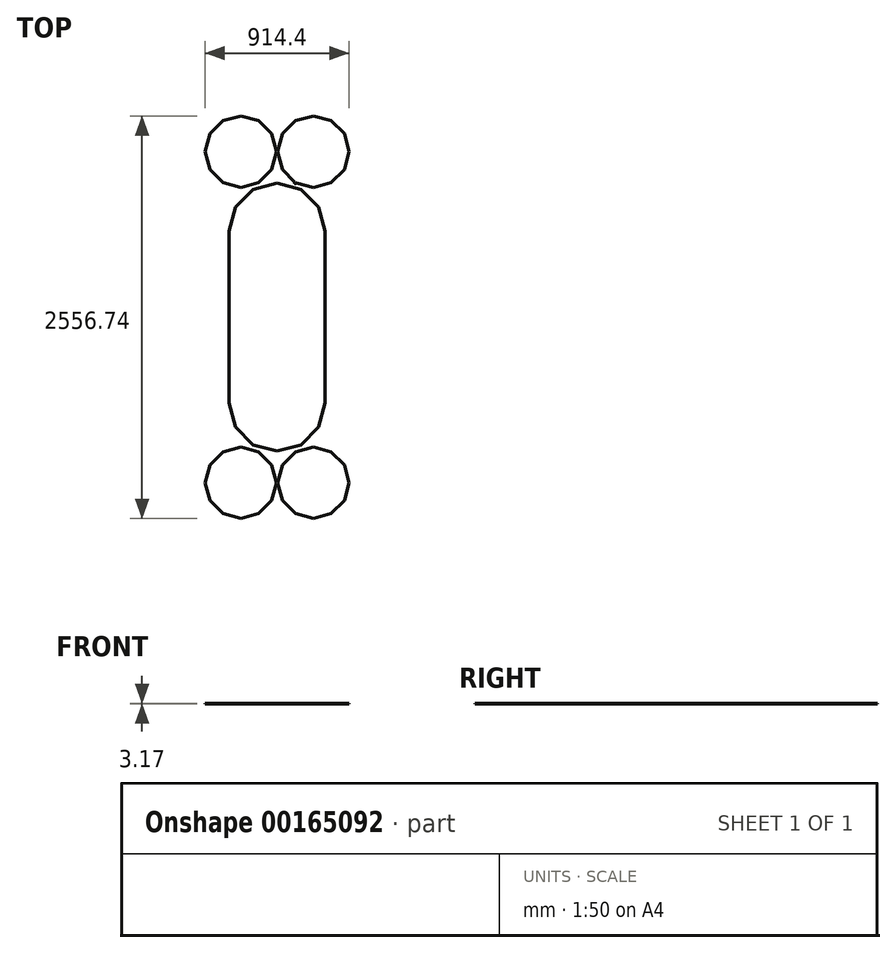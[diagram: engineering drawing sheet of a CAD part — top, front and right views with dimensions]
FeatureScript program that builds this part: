
annotation { "Feature Type Name" : "Feature", "Feature Type Description" : "" }
export const myFeature = defineFeature(function(context is Context, id is Id, definition is map)
    precondition{}
    {
        {
            var Q0;
            Q0=qCreatedBy(makeId("Top.planeOp"),FACE);
            var sketch = newSketch(context, id + "F0", { "sketchPlane" : qUnion([Q0])});
            skLineSegment(sketch, "E0", {"start": v(304.8, 0) * mm, "end": v(609.6, 0) * mm, "construction": true});
            skLineSegment(sketch, "E1", {"start": v(304.8, 0) * mm, "end": v(568.76, 152.4) * mm, "construction": true});
            skLineSegment(sketch, "E2", {"start": v(304.8, 0) * mm, "end": v(457.2, 263.96) * mm, "construction": true});
            skLineSegment(sketch, "E3", {"start": v(304.8, 0) * mm, "end": v(304.8, 304.8) * mm, "construction": true});
            skLineSegment(sketch, "E4", {"start": v(609.6, 0) * mm, "end": v(568.76, 152.4) * mm});
            skLineSegment(sketch, "E5", {"start": v(568.76, 152.4) * mm, "end": v(457.2, 263.96) * mm});
            skLineSegment(sketch, "E6", {"start": v(457.2, 263.96) * mm, "end": v(304.8, 304.8) * mm});
            skLineSegment(sketch, "E7", {"start": v(609.6, 0) * mm, "end": v(609.6, -1092.2) * mm});
            skLineSegment(sketch, "E8", {"start": v(609.6, -1092.2) * mm, "end": v(304.8, -1092.2) * mm, "construction": true});
            skLineSegment(sketch, "E9", {"start": v(304.8, -1092.2) * mm, "end": v(568.76, -1244.6) * mm, "construction": true});
            skLineSegment(sketch, "E10", {"start": v(304.8, 0) * mm, "end": v(152.4, 263.96) * mm, "construction": true});
            skLineSegment(sketch, "E11", {"start": v(304.8, 0) * mm, "end": v(40.84, 152.4) * mm, "construction": true});
            skLineSegment(sketch, "E12", {"start": v(304.8, 0) * mm, "end": v(0, 0) * mm, "construction": true});
            skLineSegment(sketch, "E13", {"start": v(304.8, -1092.2) * mm, "end": v(0, -1092.2) * mm, "construction": true});
            skLineSegment(sketch, "E14", {"start": v(304.8, 304.8) * mm, "end": v(152.4, 263.96) * mm});
            skLineSegment(sketch, "E15", {"start": v(152.4, 263.96) * mm, "end": v(40.84, 152.4) * mm});
            skLineSegment(sketch, "E16", {"start": v(40.84, 152.4) * mm, "end": v(0, 0) * mm});
            skLineSegment(sketch, "E17", {"start": v(0, 0) * mm, "end": v(0, -1092.2) * mm});
            skLineSegment(sketch, "E18", {"start": v(304.8, -1092.2) * mm, "end": v(457.2, -1356.16) * mm, "construction": true});
            skLineSegment(sketch, "E19", {"start": v(304.8, -1092.2) * mm, "end": v(304.8, -1397) * mm, "construction": true});
            skLineSegment(sketch, "E20", {"start": v(304.8, -1092.2) * mm, "end": v(152.4, -1356.16) * mm, "construction": true});
            skLineSegment(sketch, "E21", {"start": v(304.8, -1092.2) * mm, "end": v(40.84, -1244.6) * mm, "construction": true});
            skLineSegment(sketch, "E22", {"start": v(0, -1092.2) * mm, "end": v(40.84, -1244.6) * mm});
            skLineSegment(sketch, "E23", {"start": v(40.84, -1244.6) * mm, "end": v(152.4, -1356.16) * mm});
            skLineSegment(sketch, "E24", {"start": v(152.4, -1356.16) * mm, "end": v(304.8, -1397) * mm});
            skLineSegment(sketch, "E25", {"start": v(304.8, -1397) * mm, "end": v(457.2, -1356.16) * mm});
            skLineSegment(sketch, "E26", {"start": v(457.2, -1356.16) * mm, "end": v(568.76, -1244.6) * mm});
            skLineSegment(sketch, "E27", {"start": v(568.76, -1244.6) * mm, "end": v(609.6, -1092.2) * mm});
            skLineSegment(sketch, "E28", {"start": v(74.61, 505.26) * mm, "end": v(301.63, 505.26) * mm, "construction": true});
            skLineSegment(sketch, "E29", {"start": v(74.61, 505.26) * mm, "end": v(271.21, 618.77) * mm, "construction": true});
            skLineSegment(sketch, "E30", {"start": v(74.61, 505.26) * mm, "end": v(188.12, 701.86) * mm, "construction": true});
            skLineSegment(sketch, "E31", {"start": v(74.61, 505.26) * mm, "end": v(74.61, 732.27) * mm, "construction": true});
            skLineSegment(sketch, "E32", {"start": v(301.62, 505.26) * mm, "end": v(271.21, 618.77) * mm});
            skLineSegment(sketch, "E33", {"start": v(271.21, 618.77) * mm, "end": v(188.12, 701.86) * mm});
            skLineSegment(sketch, "E34", {"start": v(188.12, 701.86) * mm, "end": v(74.61, 732.27) * mm});
            skLineSegment(sketch, "E35", {"start": v(301.63, 505.26) * mm, "end": v(301.63, 505.26) * mm});
            skLineSegment(sketch, "E36", {"start": v(301.63, 505.26) * mm, "end": v(74.61, 505.26) * mm, "construction": true});
            skLineSegment(sketch, "E37", {"start": v(74.61, 505.26) * mm, "end": v(271.21, 391.76) * mm, "construction": true});
            skLineSegment(sketch, "E38", {"start": v(74.61, 505.26) * mm, "end": v(-38.9, 701.86) * mm, "construction": true});
            skLineSegment(sketch, "E39", {"start": v(74.61, 505.26) * mm, "end": v(-121.99, 618.77) * mm, "construction": true});
            skLineSegment(sketch, "E40", {"start": v(74.61, 505.26) * mm, "end": v(-152.4, 505.26) * mm, "construction": true});
            skLineSegment(sketch, "E41", {"start": v(74.61, 732.27) * mm, "end": v(-38.9, 701.86) * mm});
            skLineSegment(sketch, "E42", {"start": v(-38.9, 701.86) * mm, "end": v(-121.99, 618.77) * mm});
            skLineSegment(sketch, "E43", {"start": v(-121.99, 618.77) * mm, "end": v(-152.4, 505.26) * mm});
            skLineSegment(sketch, "E44", {"start": v(-152.4, 505.26) * mm, "end": v(-152.4, 505.26) * mm});
            skLineSegment(sketch, "E45", {"start": v(74.61, 505.26) * mm, "end": v(188.12, 308.66) * mm, "construction": true});
            skLineSegment(sketch, "E46", {"start": v(74.61, 505.26) * mm, "end": v(74.61, 278.25) * mm, "construction": true});
            skLineSegment(sketch, "E47", {"start": v(74.61, 505.26) * mm, "end": v(-38.9, 308.66) * mm, "construction": true});
            skLineSegment(sketch, "E48", {"start": v(74.61, 505.26) * mm, "end": v(-121.99, 391.76) * mm, "construction": true});
            skLineSegment(sketch, "E49", {"start": v(-152.4, 505.26) * mm, "end": v(-121.99, 391.76) * mm});
            skLineSegment(sketch, "E50", {"start": v(-121.99, 391.76) * mm, "end": v(-38.9, 308.66) * mm});
            skLineSegment(sketch, "E51", {"start": v(-38.9, 308.66) * mm, "end": v(74.61, 278.25) * mm});
            skLineSegment(sketch, "E52", {"start": v(74.61, 278.25) * mm, "end": v(188.12, 308.66) * mm});
            skLineSegment(sketch, "E53", {"start": v(188.12, 308.66) * mm, "end": v(271.21, 391.76) * mm});
            skLineSegment(sketch, "E54", {"start": v(271.21, 391.76) * mm, "end": v(301.63, 505.26) * mm});
            skLineSegment(sketch, "E55", {"start": v(534.99, 505.26) * mm, "end": v(762, 505.26) * mm, "construction": true});
            skLineSegment(sketch, "E56", {"start": v(534.99, 505.26) * mm, "end": v(731.59, 618.77) * mm, "construction": true});
            skLineSegment(sketch, "E57", {"start": v(534.99, 505.26) * mm, "end": v(648.5, 701.86) * mm, "construction": true});
            skLineSegment(sketch, "E58", {"start": v(534.99, 505.26) * mm, "end": v(534.99, 732.27) * mm, "construction": true});
            skLineSegment(sketch, "E59", {"start": v(762, 505.26) * mm, "end": v(731.59, 618.77) * mm});
            skLineSegment(sketch, "E60", {"start": v(731.59, 618.77) * mm, "end": v(648.5, 701.86) * mm});
            skLineSegment(sketch, "E61", {"start": v(648.5, 701.86) * mm, "end": v(534.99, 732.27) * mm});
            skLineSegment(sketch, "E62", {"start": v(762, 505.26) * mm, "end": v(762, 505.26) * mm});
            skLineSegment(sketch, "E63", {"start": v(762, 505.26) * mm, "end": v(534.99, 505.26) * mm, "construction": true});
            skLineSegment(sketch, "E64", {"start": v(534.99, 505.26) * mm, "end": v(731.59, 391.76) * mm, "construction": true});
            skLineSegment(sketch, "E65", {"start": v(534.99, 505.26) * mm, "end": v(421.48, 701.86) * mm, "construction": true});
            skLineSegment(sketch, "E66", {"start": v(534.99, 505.26) * mm, "end": v(338.39, 618.77) * mm, "construction": true});
            skLineSegment(sketch, "E67", {"start": v(534.99, 505.26) * mm, "end": v(307.98, 505.26) * mm, "construction": true});
            skLineSegment(sketch, "E68", {"start": v(534.99, 732.27) * mm, "end": v(421.48, 701.86) * mm});
            skLineSegment(sketch, "E69", {"start": v(421.48, 701.86) * mm, "end": v(338.39, 618.77) * mm});
            skLineSegment(sketch, "E70", {"start": v(338.39, 618.77) * mm, "end": v(307.98, 505.26) * mm});
            skLineSegment(sketch, "E71", {"start": v(307.98, 505.26) * mm, "end": v(307.98, 505.26) * mm});
            skLineSegment(sketch, "E72", {"start": v(534.99, 505.26) * mm, "end": v(648.5, 308.66) * mm, "construction": true});
            skLineSegment(sketch, "E73", {"start": v(534.99, 505.26) * mm, "end": v(534.99, 278.25) * mm, "construction": true});
            skLineSegment(sketch, "E74", {"start": v(534.99, 505.26) * mm, "end": v(421.48, 308.66) * mm, "construction": true});
            skLineSegment(sketch, "E75", {"start": v(534.99, 505.26) * mm, "end": v(338.39, 391.76) * mm, "construction": true});
            skLineSegment(sketch, "E76", {"start": v(307.98, 505.26) * mm, "end": v(338.39, 391.76) * mm});
            skLineSegment(sketch, "E77", {"start": v(338.39, 391.76) * mm, "end": v(421.48, 308.66) * mm});
            skLineSegment(sketch, "E78", {"start": v(421.48, 308.66) * mm, "end": v(534.99, 278.25) * mm});
            skLineSegment(sketch, "E79", {"start": v(534.99, 278.25) * mm, "end": v(648.5, 308.66) * mm});
            skLineSegment(sketch, "E80", {"start": v(648.5, 308.66) * mm, "end": v(731.59, 391.76) * mm});
            skLineSegment(sketch, "E81", {"start": v(731.59, 391.76) * mm, "end": v(762, 505.26) * mm});
            skLineSegment(sketch, "E82", {"start": v(534.99, -1597.46) * mm, "end": v(731.59, -1483.96) * mm, "construction": true});
            skLineSegment(sketch, "E83", {"start": v(534.99, -1597.46) * mm, "end": v(648.5, -1400.86) * mm, "construction": true});
            skLineSegment(sketch, "E84", {"start": v(534.99, -1597.46) * mm, "end": v(534.99, -1370.45) * mm, "construction": true});
            skLineSegment(sketch, "E85", {"start": v(762, -1597.46) * mm, "end": v(731.59, -1483.96) * mm});
            skLineSegment(sketch, "E86", {"start": v(731.59, -1483.96) * mm, "end": v(648.5, -1400.86) * mm});
            skLineSegment(sketch, "E87", {"start": v(648.5, -1400.86) * mm, "end": v(534.99, -1370.45) * mm});
            skLineSegment(sketch, "E88", {"start": v(762, -1597.46) * mm, "end": v(762, -1597.46) * mm});
            skLineSegment(sketch, "E89", {"start": v(762, -1597.46) * mm, "end": v(534.99, -1597.46) * mm, "construction": true});
            skLineSegment(sketch, "E90", {"start": v(534.99, -1597.46) * mm, "end": v(731.59, -1710.97) * mm, "construction": true});
            skLineSegment(sketch, "E91", {"start": v(534.99, -1597.46) * mm, "end": v(421.48, -1400.86) * mm, "construction": true});
            skLineSegment(sketch, "E92", {"start": v(534.99, -1597.46) * mm, "end": v(338.39, -1483.96) * mm, "construction": true});
            skLineSegment(sketch, "E93", {"start": v(534.99, -1597.46) * mm, "end": v(307.98, -1597.46) * mm, "construction": true});
            skLineSegment(sketch, "E94", {"start": v(534.99, -1370.45) * mm, "end": v(421.48, -1400.86) * mm});
            skLineSegment(sketch, "E95", {"start": v(421.48, -1400.86) * mm, "end": v(338.39, -1483.96) * mm});
            skLineSegment(sketch, "E96", {"start": v(338.39, -1483.96) * mm, "end": v(307.97, -1597.46) * mm});
            skLineSegment(sketch, "E97", {"start": v(307.98, -1597.46) * mm, "end": v(307.98, -1597.46) * mm});
            skLineSegment(sketch, "E98", {"start": v(534.99, -1597.46) * mm, "end": v(648.5, -1794.06) * mm, "construction": true});
            skLineSegment(sketch, "E99", {"start": v(534.99, -1597.46) * mm, "end": v(534.99, -1824.47) * mm, "construction": true});
            skLineSegment(sketch, "E100", {"start": v(534.99, -1597.46) * mm, "end": v(421.48, -1794.06) * mm, "construction": true});
            skLineSegment(sketch, "E101", {"start": v(534.99, -1597.46) * mm, "end": v(338.39, -1710.97) * mm, "construction": true});
            skLineSegment(sketch, "E102", {"start": v(307.98, -1597.46) * mm, "end": v(338.39, -1710.97) * mm});
            skLineSegment(sketch, "E103", {"start": v(338.39, -1710.97) * mm, "end": v(421.48, -1794.06) * mm});
            skLineSegment(sketch, "E104", {"start": v(421.48, -1794.06) * mm, "end": v(534.99, -1824.47) * mm});
            skLineSegment(sketch, "E105", {"start": v(534.99, -1824.47) * mm, "end": v(648.5, -1794.06) * mm});
            skLineSegment(sketch, "E106", {"start": v(648.5, -1794.06) * mm, "end": v(731.59, -1710.97) * mm});
            skLineSegment(sketch, "E107", {"start": v(731.59, -1710.97) * mm, "end": v(762, -1597.46) * mm});
            skLineSegment(sketch, "E108", {"start": v(74.61, -1597.46) * mm, "end": v(271.21, -1483.96) * mm, "construction": true});
            skLineSegment(sketch, "E109", {"start": v(74.61, -1597.46) * mm, "end": v(188.12, -1400.86) * mm, "construction": true});
            skLineSegment(sketch, "E110", {"start": v(74.61, -1597.46) * mm, "end": v(74.61, -1370.45) * mm, "construction": true});
            skLineSegment(sketch, "E111", {"start": v(301.63, -1597.46) * mm, "end": v(271.21, -1483.96) * mm});
            skLineSegment(sketch, "E112", {"start": v(271.21, -1483.96) * mm, "end": v(188.12, -1400.86) * mm});
            skLineSegment(sketch, "E113", {"start": v(188.12, -1400.86) * mm, "end": v(74.61, -1370.45) * mm});
            skLineSegment(sketch, "E114", {"start": v(301.63, -1597.46) * mm, "end": v(301.63, -1597.46) * mm});
            skLineSegment(sketch, "E115", {"start": v(301.63, -1597.46) * mm, "end": v(74.61, -1597.46) * mm, "construction": true});
            skLineSegment(sketch, "E116", {"start": v(74.61, -1597.46) * mm, "end": v(271.21, -1710.97) * mm, "construction": true});
            skLineSegment(sketch, "E117", {"start": v(74.61, -1597.46) * mm, "end": v(-38.9, -1400.86) * mm, "construction": true});
            skLineSegment(sketch, "E118", {"start": v(74.61, -1597.46) * mm, "end": v(-121.99, -1483.96) * mm, "construction": true});
            skLineSegment(sketch, "E119", {"start": v(74.61, -1597.46) * mm, "end": v(-152.4, -1597.46) * mm, "construction": true});
            skLineSegment(sketch, "E120", {"start": v(74.61, -1370.45) * mm, "end": v(-38.9, -1400.86) * mm});
            skLineSegment(sketch, "E121", {"start": v(-38.9, -1400.86) * mm, "end": v(-121.99, -1483.96) * mm});
            skLineSegment(sketch, "E122", {"start": v(-121.99, -1483.96) * mm, "end": v(-152.4, -1597.46) * mm});
            skLineSegment(sketch, "E123", {"start": v(-152.4, -1597.46) * mm, "end": v(-152.4, -1597.46) * mm});
            skLineSegment(sketch, "E124", {"start": v(74.61, -1597.46) * mm, "end": v(188.12, -1794.06) * mm, "construction": true});
            skLineSegment(sketch, "E125", {"start": v(74.61, -1597.46) * mm, "end": v(74.61, -1824.47) * mm, "construction": true});
            skLineSegment(sketch, "E126", {"start": v(74.61, -1597.46) * mm, "end": v(-38.9, -1794.06) * mm, "construction": true});
            skLineSegment(sketch, "E127", {"start": v(74.61, -1597.46) * mm, "end": v(-121.99, -1710.97) * mm, "construction": true});
            skLineSegment(sketch, "E128", {"start": v(-152.4, -1597.46) * mm, "end": v(-121.99, -1710.97) * mm});
            skLineSegment(sketch, "E129", {"start": v(-121.99, -1710.97) * mm, "end": v(-38.9, -1794.06) * mm});
            skLineSegment(sketch, "E130", {"start": v(-38.9, -1794.06) * mm, "end": v(74.61, -1824.47) * mm});
            skLineSegment(sketch, "E131", {"start": v(74.61, -1824.47) * mm, "end": v(188.12, -1794.06) * mm});
            skLineSegment(sketch, "E132", {"start": v(188.12, -1794.06) * mm, "end": v(271.21, -1710.97) * mm});
            skLineSegment(sketch, "E133", {"start": v(271.21, -1710.97) * mm, "end": v(301.63, -1597.46) * mm});
            skLineSegment(sketch, "E134", {"start": v(304.8, 304.8) * mm, "end": v(304.8, 505.26) * mm, "construction": true});
            skLineSegment(sketch, "E135", {"start": v(301.63, 505.26) * mm, "end": v(307.98, 505.26) * mm, "construction": true});
            skLineSegment(sketch, "E136", {"start": v(304.8, -1397) * mm, "end": v(304.8, -1597.46) * mm, "construction": true});
            skLineSegment(sketch, "E137", {"start": v(301.63, -1597.46) * mm, "end": v(307.98, -1597.46) * mm, "construction": true});
            skLineSegment(sketch, "E138", {"start": v(762, -1597.46) * mm, "end": v(762, 505.26) * mm, "construction": true});
            skLineSegment(sketch, "E139", {"start": v(-152.4, 505.26) * mm, "end": v(-152.4, -1597.46) * mm, "construction": true});
            skCircle(sketch, "E140", {"center": v(421.48, 308.66) * mm, "radius": 6.35 * mm});
            skLineSegment(sketch, "E141", {"start": v(304.8, -1092.2) * mm, "end": v(304.8, 0) * mm, "construction": true});
            skSolve(sketch);
        }
        {
            var Q0;
            Q0=qSketchRegion(id+"F0",true);
            extrude(context, id + "F1", {"entities" : qUnion([Q0]), "depth" : 3.17 * mm});
        }
    });
